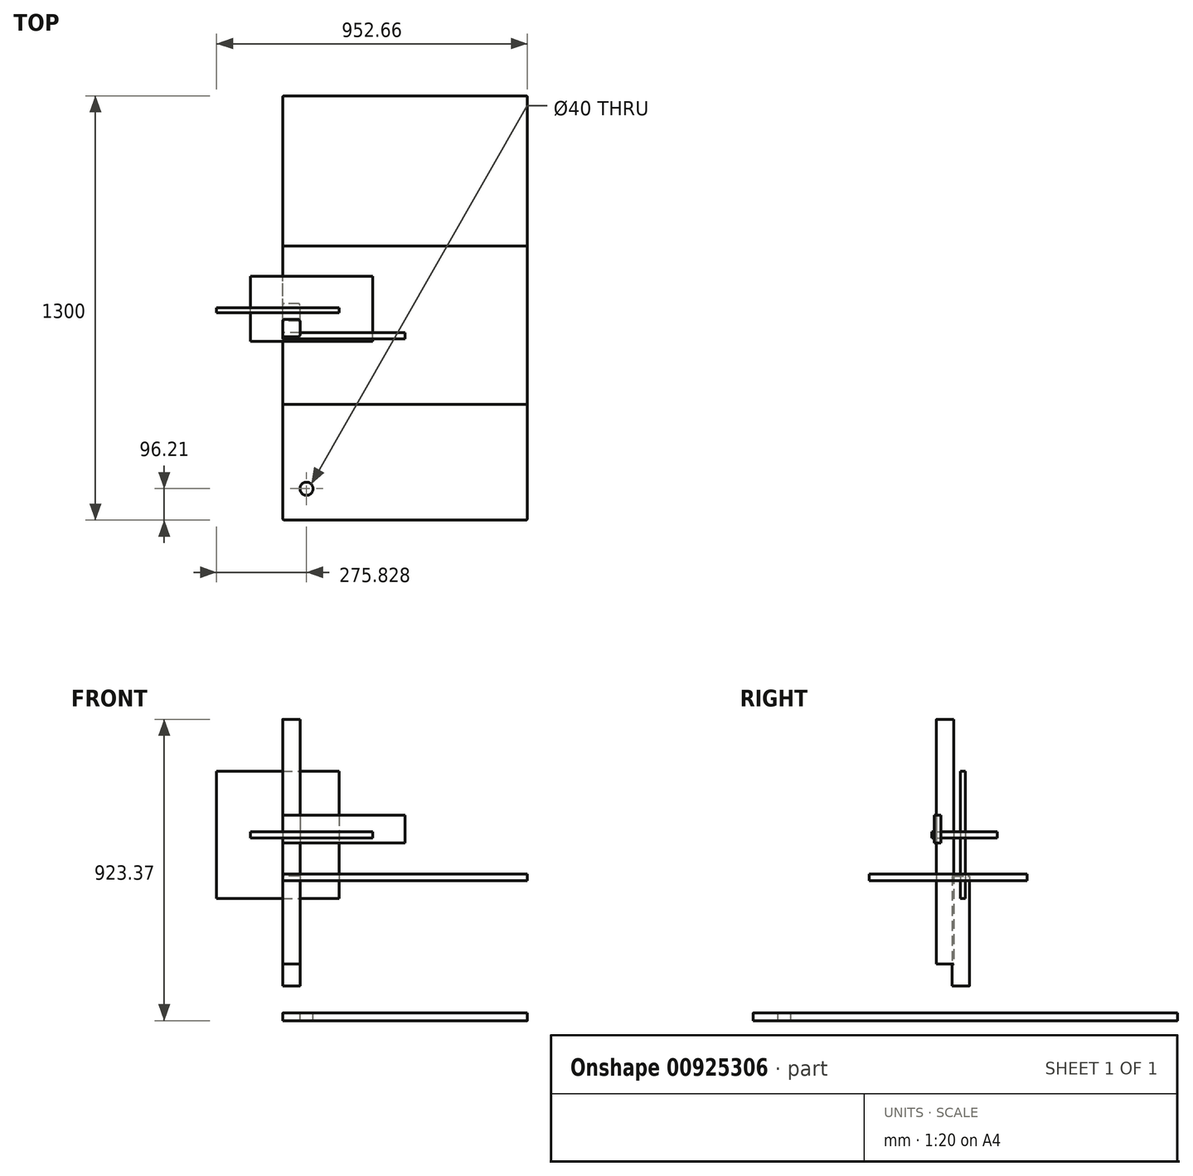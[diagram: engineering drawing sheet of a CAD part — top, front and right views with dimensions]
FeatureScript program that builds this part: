
annotation { "Feature Type Name" : "Feature", "Feature Type Description" : "" }
export const myFeature = defineFeature(function(context is Context, id is Id, definition is map)
    precondition{}
    {
        {
            var Q0;
            Q0=qCreatedBy(makeId("Right.planeOp"),FACE);
            var sketch = newSketch(context, id + "F0", { "sketchPlane" : qUnion([Q0])});
            skLineSegment(sketch, "E0.bottom", {"start": v(-650.61, -536.2) * mm, "end": v(649.39, -536.2) * mm});
            skLineSegment(sketch, "E0.top", {"start": v(-650.61, -559.2) * mm, "end": v(649.39, -559.2) * mm});
            skLineSegment(sketch, "E0.left", {"start": v(-650.61, -536.2) * mm, "end": v(-650.61, -559.2) * mm});
            skLineSegment(sketch, "E0.right", {"start": v(649.39, -536.2) * mm, "end": v(649.39, -559.2) * mm});
            skLineSegment(sketch, "E1.bottom", {"start": v(-420.61, -559.2) * mm, "end": v(-435.61, -559.2) * mm});
            skLineSegment(sketch, "E1.top", {"start": v(-420.61, -949.2) * mm, "end": v(-435.61, -949.2) * mm});
            skLineSegment(sketch, "E1.left", {"start": v(-420.61, -559.2) * mm, "end": v(-420.61, -949.2) * mm});
            skLineSegment(sketch, "E1.right", {"start": v(-435.61, -559.2) * mm, "end": v(-435.61, -949.2) * mm});
            skLineSegment(sketch, "E2.bottom", {"start": v(-435.61, -929.2) * mm, "end": v(-635.61, -929.2) * mm});
            skLineSegment(sketch, "E2.top", {"start": v(-435.61, -949.2) * mm, "end": v(-635.61, -949.2) * mm});
            skLineSegment(sketch, "E2.left", {"start": v(-435.61, -929.2) * mm, "end": v(-435.61, -949.2) * mm});
            skLineSegment(sketch, "E2.right", {"start": v(-635.61, -929.2) * mm, "end": v(-635.61, -949.2) * mm});
            skLineSegment(sketch, "E3.bottom", {"start": v(-650.61, -559.2) * mm, "end": v(-635.61, -559.2) * mm});
            skLineSegment(sketch, "E3.top", {"start": v(-650.61, -949.2) * mm, "end": v(-635.61, -949.2) * mm});
            skLineSegment(sketch, "E3.left", {"start": v(-650.61, -559.2) * mm, "end": v(-650.61, -949.2) * mm});
            skLineSegment(sketch, "E3.right", {"start": v(-635.61, -559.2) * mm, "end": v(-635.61, -949.2) * mm});
            skLineSegment(sketch, "E4.bottom", {"start": v(-399.37, -559.2) * mm, "end": v(-417.37, -559.2) * mm});
            skLineSegment(sketch, "E5.bottom", {"start": v(-420.61, -644.2) * mm, "end": v(549.39, -644.2) * mm});
            skLineSegment(sketch, "E5.top", {"start": v(-420.61, -624.2) * mm, "end": v(549.39, -624.2) * mm});
            skLineSegment(sketch, "E5.left", {"start": v(-420.61, -644.2) * mm, "end": v(-420.61, -624.2) * mm});
            skLineSegment(sketch, "E5.right", {"start": v(549.39, -644.2) * mm, "end": v(549.39, -624.2) * mm});
            skLineSegment(sketch, "E6.bottom", {"start": v(549.39, -644.2) * mm, "end": v(569.39, -644.2) * mm});
            skLineSegment(sketch, "E6.top", {"start": v(549.39, -559.2) * mm, "end": v(569.39, -559.2) * mm});
            skLineSegment(sketch, "E6.left", {"start": v(549.39, -644.2) * mm, "end": v(549.39, -559.2) * mm});
            skLineSegment(sketch, "E6.right", {"start": v(569.39, -644.2) * mm, "end": v(569.39, -559.2) * mm});
            skSolve(sketch);
        }
        {
            var Q0;
            Q0=makeQuery(id+"F0.imprint","IMPRINT",FACE,{"disambiguationData":[TD([[makeQuery(id+"F0.imprint","IMPRINT",EDGE,{"derivedFrom":sQuery(id+"F0.wireOp",EDGE,"E0.bottom")}),-1.0]])]});
            extrude(context, id + "F1", {"entities" : qUnion([Q0]), "depth" : 750 * mm, "offsetDistance" : 25 * mm});
        }
        {
            var Q0;
            Q0=qCreatedBy(makeId("Right.planeOp"),FACE);
            var sketch = newSketch(context, id + "F2", { "sketchPlane" : qUnion([Q0])});
            skLineSegment(sketch, "E7.bottom", {"start": v(-88.86, 364.18) * mm, "end": v(-35.86, 364.18) * mm});
            skLineSegment(sketch, "E7.top", {"start": v(-88.86, -385.82) * mm, "end": v(-35.86, -385.82) * mm});
            skLineSegment(sketch, "E7.left", {"start": v(-88.86, 364.18) * mm, "end": v(-88.86, -385.82) * mm});
            skLineSegment(sketch, "E7.right", {"start": v(-35.86, 364.18) * mm, "end": v(-35.86, -385.82) * mm});
            skLineSegment(sketch, "E8.left", {"start": v(-88.86, -10.82) * mm, "end": v(-88.86, 4.18) * mm});
            skLineSegment(sketch, "E9.left", {"start": v(-88.86, 364.18) * mm, "end": v(-88.86, 341.53) * mm});
            skLineSegment(sketch, "E10.left", {"start": v(-88.86, 122.14) * mm, "end": v(-88.86, 142.14) * mm});
            skSolve(sketch);
        }
        {
            var Q0;
            Q0=makeQuery(id+"F2.imprint","IMPRINT",FACE,{"disambiguationData":[TD([[makeQuery(id+"F2.imprint","IMPRINT",EDGE,{"derivedFrom":sQuery(id+"F2.wireOp",EDGE,"E7.bottom")}),-1.0]])]});
            extrude(context, id + "F3", {"entities" : qUnion([Q0]), "depth" : 53 * mm, "offsetDistance" : 25 * mm});
        }
        {
            var Q0;
            Q0=qCreatedBy(makeId("Right.planeOp"),FACE);
            var sketch = newSketch(context, id + "F4", { "sketchPlane" : qUnion([Q0])});
            skLineSegment(sketch, "E11.bottom", {"start": v(-40.42, -115.93) * mm, "end": v(12.58, -115.93) * mm});
            skLineSegment(sketch, "E11.top", {"start": v(-40.42, -452.93) * mm, "end": v(12.58, -452.93) * mm});
            skLineSegment(sketch, "E11.left", {"start": v(-40.42, -115.93) * mm, "end": v(-40.42, -452.93) * mm});
            skLineSegment(sketch, "E11.right", {"start": v(12.58, -115.93) * mm, "end": v(12.58, -452.93) * mm});
            skLineSegment(sketch, "E12.left", {"start": v(-40.42, -284.43) * mm, "end": v(-40.42, -269.43) * mm});
            skLineSegment(sketch, "E13.left", {"start": v(-40.42, -115.93) * mm, "end": v(-40.42, -138.58) * mm});
            skLineSegment(sketch, "E14.left", {"start": v(-40.42, 55.03) * mm, "end": v(-40.42, 75.03) * mm});
            skSolve(sketch);
        }
        {
            var Q0;
            Q0=makeQuery(id+"F4.imprint","IMPRINT",FACE,{"disambiguationData":[TD([[makeQuery(id+"F4.imprint","IMPRINT",EDGE,{"derivedFrom":sQuery(id+"F4.wireOp",EDGE,"E11.bottom")}),-1.0]])]});
            extrude(context, id + "F5", {"entities" : qUnion([Q0]), "depth" : 53 * mm, "offsetDistance" : 25 * mm});
        }
        {
            var Q0;
            Q0=makeQuery(id+"F1.opExtrude","CAP_EDGE",EDGE,{"disambiguationData":[OSD([sQuery(id+"F0.wireOp",EDGE,"E0.left")])],"isStart":false});
            var Q1;
            Q1=makeQuery(id+"F1.opExtrude","CAP_EDGE",EDGE,{"disambiguationData":[OSD([sQuery(id+"F0.wireOp",EDGE,"E1.right")])],"isStart":false});
            var Q2;
            Q2=makeQuery(id+"F1.opExtrude","CAP_EDGE",EDGE,{"disambiguationData":[OSD([sQuery(id+"F0.wireOp",EDGE,"E3.right")])],"isStart":false});
            var Q3;
            {var subQ0=sQuery(id+"F0.wireOp",EDGE,"E1.left");Q3=makeQuery(id+"F1.opExtrude","CAP_EDGE",EDGE,{"disambiguationData":[OSD([subQ0]),TDD([makeQuery(id+"F0.imprint","IMPRINT",EDGE,{"disambiguationData":[TD([[makeQuery(id+"F0.imprint","INTERSECT",VERTEX,{"derivedFrom":[sQuery(id+"F0.wireOp",EDGE,"E0.top"),sQuery(id+"F0.wireOp",EDGE,"E1.bottom"),subQ0]}),-1.0]])],"derivedFrom":subQ0})])],"isStart":false});}
            var Q4;
            {var subQ0=sQuery(id+"F0.wireOp",EDGE,"E1.left");Q4=makeQuery(id+"F1.opExtrude","CAP_EDGE",EDGE,{"disambiguationData":[OSD([subQ0]),TDD([makeQuery(id+"F0.imprint","IMPRINT",EDGE,{"disambiguationData":[TD([[makeQuery(id+"F0.imprint","INTERSECT",VERTEX,{"derivedFrom":[sQuery(id+"F0.wireOp",EDGE,"E1.top"),subQ0]}),1.0]])],"derivedFrom":subQ0})])],"isStart":false});}
            var Q5;
            Q5=makeQuery(id+"F1.opExtrude","CAP_EDGE",EDGE,{"disambiguationData":[OSD([sQuery(id+"F0.wireOp",EDGE,"E6.right")])],"isStart":false});
            var Q6;
            Q6=makeQuery(id+"F1.opExtrude","CAP_EDGE",EDGE,{"disambiguationData":[OSD([sQuery(id+"F0.wireOp",EDGE,"E0.right")])],"isStart":false});
            var Q7;
            Q7=makeQuery(id+"F1.opExtrude","CAP_EDGE",EDGE,{"disambiguationData":[OSD([sQuery(id+"F0.wireOp",EDGE,"E6.right")])],"isStart":true});
            var Q8;
            Q8=makeQuery(id+"F1.opExtrude","CAP_EDGE",EDGE,{"disambiguationData":[OSD([sQuery(id+"F0.wireOp",EDGE,"E0.right")])],"isStart":true});
            var Q9;
            Q9=makeQuery(id+"F1.opExtrude","CAP_EDGE",EDGE,{"disambiguationData":[OSD([sQuery(id+"F0.wireOp",EDGE,"E6.left")])],"isStart":true});
            var Q10;
            {var subQ0=sQuery(id+"F0.wireOp",EDGE,"E1.left");Q10=makeQuery(id+"F1.opExtrude","CAP_EDGE",EDGE,{"disambiguationData":[OSD([subQ0]),TDD([makeQuery(id+"F0.imprint","IMPRINT",EDGE,{"disambiguationData":[TD([[makeQuery(id+"F0.imprint","INTERSECT",VERTEX,{"derivedFrom":[sQuery(id+"F0.wireOp",EDGE,"E0.top"),sQuery(id+"F0.wireOp",EDGE,"E1.bottom"),subQ0]}),-1.0]])],"derivedFrom":subQ0})])],"isStart":true});}
            var Q11;
            Q11=makeQuery(id+"F1.opExtrude","CAP_EDGE",EDGE,{"disambiguationData":[OSD([sQuery(id+"F0.wireOp",EDGE,"E1.right")])],"isStart":true});
            var Q12;
            Q12=makeQuery(id+"F1.opExtrude","CAP_EDGE",EDGE,{"disambiguationData":[OSD([sQuery(id+"F0.wireOp",EDGE,"E0.left")])],"isStart":true});
            var Q13;
            Q13=makeQuery(id+"F1.opExtrude","CAP_EDGE",EDGE,{"disambiguationData":[OSD([sQuery(id+"F0.wireOp",EDGE,"E3.right")])],"isStart":true});
            var Q14;
            {var subQ0=sQuery(id+"F0.wireOp",EDGE,"E1.left");Q14=makeQuery(id+"F1.opExtrude","CAP_EDGE",EDGE,{"disambiguationData":[OSD([subQ0]),TDD([makeQuery(id+"F0.imprint","IMPRINT",EDGE,{"disambiguationData":[TD([[makeQuery(id+"F0.imprint","INTERSECT",VERTEX,{"derivedFrom":[sQuery(id+"F0.wireOp",EDGE,"E1.top"),subQ0]}),1.0]])],"derivedFrom":subQ0})])],"isStart":true});}
            fillet(context, id + "F6", {"entities" : qUnion([Q0, Q1, Q2, Q3, Q4, Q5, Q6, Q7, Q8, Q9, Q10, Q11, Q12, Q13, Q14]), "radius" : 5 * mm, "tangentPropagation" : true, "allowEdgeOverflow" : false});
        }
        {
            var Q0;
            Q0=makeQuery(id+"F3.opExtrude","CAP_EDGE",EDGE,{"disambiguationData":[OSD([sQuery(id+"F2.wireOp",EDGE,"E7.right")])],"isStart":true});
            var Q1;
            Q1=makeQuery(id+"F3.opExtrude","CAP_EDGE",EDGE,{"disambiguationData":[OSD([sQuery(id+"F2.wireOp",EDGE,"E7.left"),sQuery(id+"F2.wireOp",EDGE,"E8.left"),sQuery(id+"F2.wireOp",EDGE,"E9.left"),sQuery(id+"F2.wireOp",EDGE,"E10.left")])],"isStart":true});
            var Q2;
            Q2=makeQuery(id+"F3.opExtrude","CAP_EDGE",EDGE,{"disambiguationData":[OSD([sQuery(id+"F2.wireOp",EDGE,"E7.left"),sQuery(id+"F2.wireOp",EDGE,"E8.left"),sQuery(id+"F2.wireOp",EDGE,"E9.left"),sQuery(id+"F2.wireOp",EDGE,"E10.left")])],"isStart":false});
            var Q3;
            Q3=makeQuery(id+"F3.opExtrude","CAP_EDGE",EDGE,{"disambiguationData":[OSD([sQuery(id+"F2.wireOp",EDGE,"E7.right")])],"isStart":false});
            fillet(context, id + "F7", {"entities" : qUnion([Q0, Q1, Q2, Q3]), "radius" : 5 * mm, "tangentPropagation" : true, "allowEdgeOverflow" : false});
        }
        {
            var Q0;
            Q0=makeQuery(id+"F5.opExtrude","CAP_EDGE",EDGE,{"disambiguationData":[OSD([sQuery(id+"F4.wireOp",EDGE,"E11.right")])],"isStart":true});
            var Q1;
            Q1=makeQuery(id+"F5.opExtrude","CAP_EDGE",EDGE,{"disambiguationData":[OSD([sQuery(id+"F4.wireOp",EDGE,"E11.left"),sQuery(id+"F4.wireOp",EDGE,"E12.left"),sQuery(id+"F4.wireOp",EDGE,"E13.left")])],"isStart":true});
            var Q2;
            Q2=makeQuery(id+"F5.opExtrude","CAP_EDGE",EDGE,{"disambiguationData":[OSD([sQuery(id+"F4.wireOp",EDGE,"E11.left"),sQuery(id+"F4.wireOp",EDGE,"E12.left"),sQuery(id+"F4.wireOp",EDGE,"E13.left")])],"isStart":false});
            var Q3;
            Q3=makeQuery(id+"F5.opExtrude","CAP_EDGE",EDGE,{"disambiguationData":[OSD([sQuery(id+"F4.wireOp",EDGE,"E11.right")])],"isStart":false});
            fillet(context, id + "F8", {"entities" : qUnion([Q0, Q1, Q2, Q3]), "radius" : 5 * mm, "tangentPropagation" : true, "allowEdgeOverflow" : false});
        }
        {
            var Q0;
            Q0=qCreatedBy(makeId("Front.planeOp"),FACE);
            var sketch = newSketch(context, id + "F9", { "sketchPlane" : qUnion([Q0])});
            skLineSegment(sketch, "E15.bottom", {"start": v(-202.66, 205.1) * mm, "end": v(172.34, 205.1) * mm});
            skLineSegment(sketch, "E15.top", {"start": v(-202.66, -184.9) * mm, "end": v(172.34, -184.9) * mm});
            skLineSegment(sketch, "E15.left", {"start": v(-202.66, 205.1) * mm, "end": v(-202.66, -184.9) * mm});
            skLineSegment(sketch, "E15.right", {"start": v(172.34, 205.1) * mm, "end": v(172.34, -184.9) * mm});
            skSolve(sketch);
        }
        {
            var Q0;
            Q0=makeQuery(id+"F9.imprint","IMPRINT",FACE,{"disambiguationData":[TD([[makeQuery(id+"F9.imprint","IMPRINT",EDGE,{"derivedFrom":sQuery(id+"F9.wireOp",EDGE,"E15.bottom")}),-1.0]])]});
            extrude(context, id + "F10", {"entities" : qUnion([Q0]), "depth" : 15 * mm, "offsetDistance" : 25 * mm});
        }
        {
            var Q0;
            Q0=qCreatedBy(makeId("Top.planeOp"),FACE);
            var sketch = newSketch(context, id + "F11", { "sketchPlane" : qUnion([Q0])});
            skLineSegment(sketch, "E16.bottom", {"start": v(-98.7, -102.95) * mm, "end": v(276.3, -102.95) * mm});
            skLineSegment(sketch, "E16.top", {"start": v(-98.7, 97.05) * mm, "end": v(276.3, 97.05) * mm});
            skLineSegment(sketch, "E16.left", {"start": v(-98.7, -102.95) * mm, "end": v(-98.7, 97.05) * mm});
            skLineSegment(sketch, "E16.right", {"start": v(276.3, -102.95) * mm, "end": v(276.3, 97.05) * mm});
            skSolve(sketch);
        }
        {
            var Q0;
            Q0=makeQuery(id+"F11.imprint","IMPRINT",FACE,{"disambiguationData":[TD([[makeQuery(id+"F11.imprint","IMPRINT",EDGE,{"derivedFrom":sQuery(id+"F11.wireOp",EDGE,"E16.bottom")}),1.0]])]});
            extrude(context, id + "F12", {"entities" : qUnion([Q0]), "depth" : 20 * mm, "offsetDistance" : 25 * mm});
        }
        {
            var Q0;
            Q0=qCreatedBy(makeId("Right.planeOp"),FACE);
            var sketch = newSketch(context, id + "F13", { "sketchPlane" : qUnion([Q0])});
            skLineSegment(sketch, "E17.bottom", {"start": v(-295.5, -110.14) * mm, "end": v(189.5, -110.14) * mm});
            skLineSegment(sketch, "E17.top", {"start": v(-295.5, -130.14) * mm, "end": v(189.5, -130.14) * mm});
            skLineSegment(sketch, "E17.left", {"start": v(-295.5, -110.14) * mm, "end": v(-295.5, -130.14) * mm});
            skLineSegment(sketch, "E17.right", {"start": v(189.5, -110.14) * mm, "end": v(189.5, -130.14) * mm});
            skSolve(sketch);
        }
        {
            var Q0;
            Q0=makeQuery(id+"F13.imprint","IMPRINT",FACE,{"disambiguationData":[TD([[makeQuery(id+"F13.imprint","IMPRINT",EDGE,{"derivedFrom":sQuery(id+"F13.wireOp",EDGE,"E17.bottom")}),-1.0]])]});
            extrude(context, id + "F14", {"entities" : qUnion([Q0]), "depth" : 750 * mm, "offsetDistance" : 25 * mm});
        }
        {
            var Q0;
            Q0=makeQuery(id+"F1.opExtrude","SWEPT_FACE",FACE,{"disambiguationData":[OSD([sQuery(id+"F0.wireOp",EDGE,"E0.bottom")])]});
            var sketch = newSketch(context, id + "F15", { "sketchPlane" : qUnion([Q0])});
            skCircle(sketch, "E18", {"center": v(73.17, -554.4) * mm, "radius": 33.9 * mm});
            skSolve(sketch);
        }
        {
            var Q0;
            Q0=sQuery(id+"F15.wireOp",VERTEX,"E18.center");
            var Q1;
            Q1=makeQuery(id+"F1.opExtrude","SWEPT_BODY",BODY,{"disambiguationData":[OSD([sQuery(id+"F0.wireOp",EDGE,"E0.bottom"),sQuery(id+"F0.wireOp",EDGE,"E0.top"),sQuery(id+"F0.wireOp",EDGE,"E0.left"),sQuery(id+"F0.wireOp",EDGE,"E0.right")])]});
            hole(context, id + "F16", {"style" : HoleStyle.C_BORE, "endStyle" : HoleEndStyle.BLIND, "holeDiameter" : 40 * mm, "cBoreDiameter" : 40 * mm, "cBoreDepth" : 5 * mm, "majorDiameter" : 5 * mm, "holeDepth" : 40 * mm, "isTappedThrough" : true, "tappedDepth" : 12 * mm, "tapClearance" : 3, "locations" : qUnion([Q0]), "scope" : qUnion([Q1])});
        }
        {
            var Q0;
            Q0=qCreatedBy(makeId("Right.planeOp"),FACE);
            var sketch = newSketch(context, id + "F17", { "sketchPlane" : qUnion([Q0])});
            skLineSegment(sketch, "E19.bottom", {"start": v(-95.7, 70.45) * mm, "end": v(-75.7, 70.45) * mm});
            skLineSegment(sketch, "E19.top", {"start": v(-95.7, -14.55) * mm, "end": v(-75.7, -14.55) * mm});
            skLineSegment(sketch, "E19.left", {"start": v(-95.7, 70.45) * mm, "end": v(-95.7, -14.55) * mm});
            skLineSegment(sketch, "E19.right", {"start": v(-75.7, 70.45) * mm, "end": v(-75.7, -14.55) * mm});
            skSolve(sketch);
        }
        {
            var Q0;
            Q0=makeQuery(id+"F17.imprint","IMPRINT",FACE,{"disambiguationData":[TD([[makeQuery(id+"F17.imprint","IMPRINT",EDGE,{"derivedFrom":sQuery(id+"F17.wireOp",EDGE,"E19.bottom")}),-1.0]])]});
            extrude(context, id + "F18", {"entities" : qUnion([Q0]), "depth" : 375 * mm, "offsetDistance" : 25 * mm});
        }
    });
